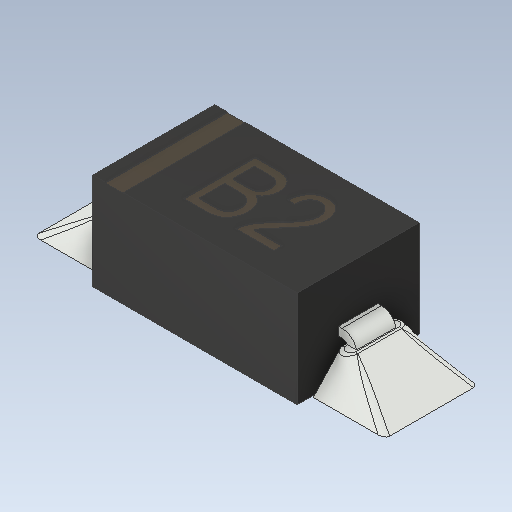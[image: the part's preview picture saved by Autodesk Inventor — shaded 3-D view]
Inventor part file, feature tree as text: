
AUTODESK INVENTOR PART (.ipt)
format: ipt  version: 2020.1 (Build 241239000, 239)  size: 365,056 bytes
history: native  units: mm
features: fillet x1
ambient origin geometry x8: Origin, YZ Plane, XZ Plane, XY Plane, X Axis, Y Axis, Z Axis, Center Point
bodies: Solid1 (feature_tree)
feature tree (1):
  fillet  "Fillet9"  [1 undecoded]
note: 1 required parameter value undecoded (feature->parameter linkage not recoverable at this tier; creation-order binding heuristic only, values carry confidence <= 0.55)
